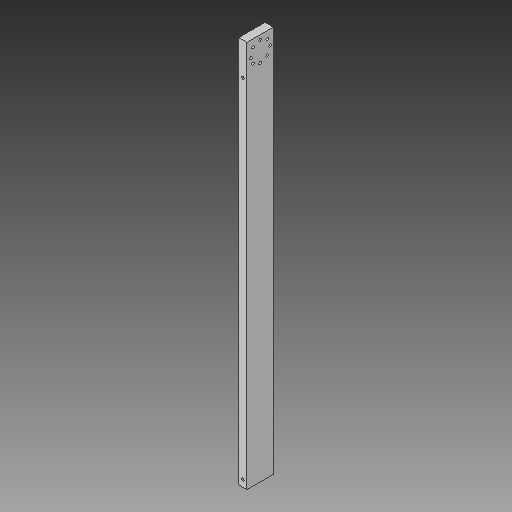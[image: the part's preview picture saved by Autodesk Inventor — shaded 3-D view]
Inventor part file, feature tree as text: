
AUTODESK INVENTOR PART (.ipt)
format: ipt  version: 2019 (Build 230136000, 136)  size: 129,024 bytes
history: native  units: in
note: dims shown in document units (in); Inventor stores cm internally (conversion verified against a paired STEP export)
features: sketch x3, hole x2, extrude x1
ambient origin geometry x8: Origin, YZ Plane, XZ Plane, XY Plane, X Axis, Y Axis, Z Axis, Center Point
bodies: Solid1 (feature_tree)
feature tree (6):
  extrude  "Extrusion1"  Depth=14.75in
  sketch  "Sketch2"  dims[d2=1.0in d3=0.0in d4=0.25in]
  hole  "Hole1"  [1 undecoded]
  hole  "Hole2"  [1 undecoded]
  sketch  "Sketch1"  dims[d0=0.312in d1=14.75in]
  sketch  "Sketch3"  dims[d5=0.14in d6=1.25in d7=0.14in d10=0.104in d11=1.0in d12=0.375in d13=0.25in d14=0.5635in d15=1.0in d16=0.8108in d24=0.107in d25=0.3in d26=0.375in d27=0.25in d28=0.5635in d29=1.0in d30=0.8108in d35=0.55in d36=0.77in d37=3.1496in d39=360.0deg]
note: 2 required parameter values undecoded (feature->parameter linkage not recoverable at this tier; creation-order binding heuristic only, values carry confidence <= 0.55)
